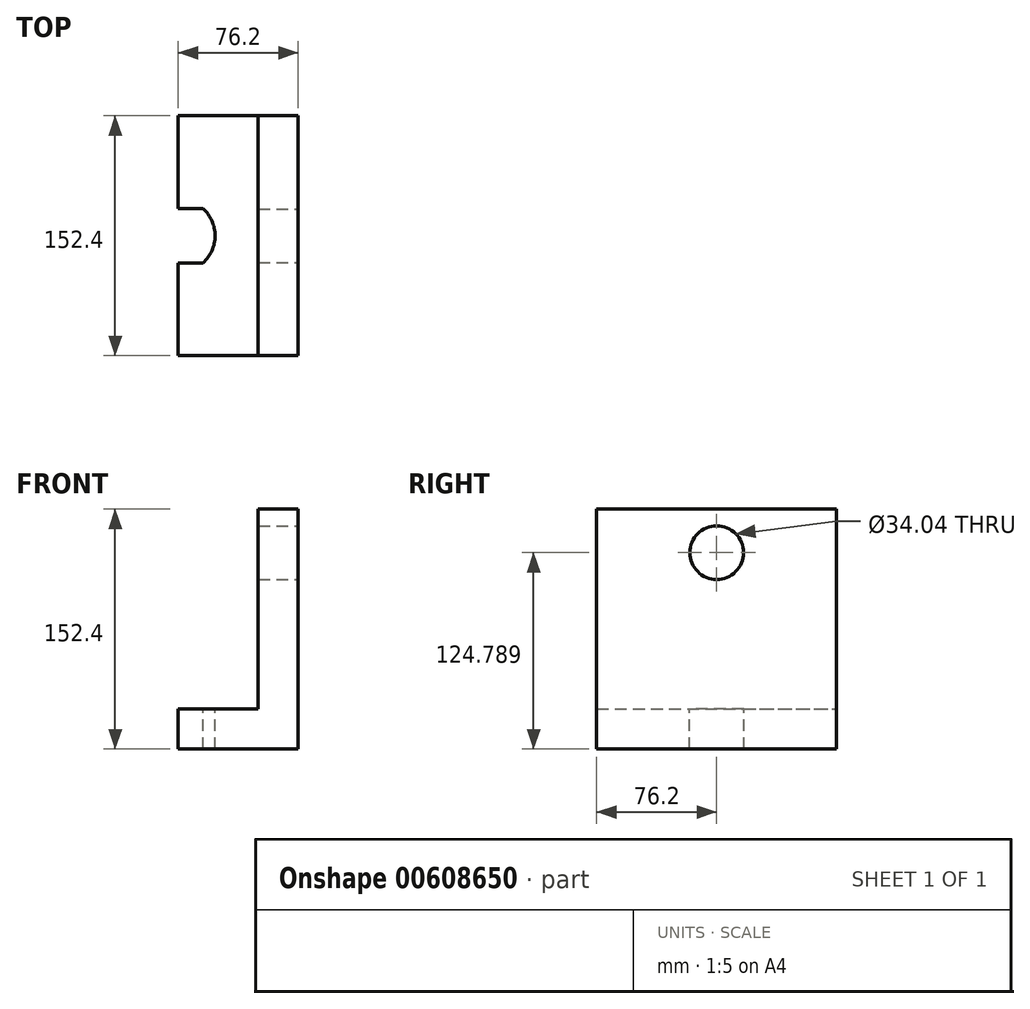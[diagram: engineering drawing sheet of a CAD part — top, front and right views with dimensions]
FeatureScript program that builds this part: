
annotation { "Feature Type Name" : "Feature", "Feature Type Description" : "" }
export const myFeature = defineFeature(function(context is Context, id is Id, definition is map)
    precondition{}
    {
        {
            var Q0;
            Q0=qCreatedBy(makeId("Front.planeOp"),FACE);
            var sketch = newSketch(context, id + "F0", { "sketchPlane" : qUnion([Q0])});
            skLineSegment(sketch, "E0", {"start": v(0, 152.4) * mm, "end": v(-25.4, 152.4) * mm});
            skLineSegment(sketch, "E1", {"start": v(-25.4, 25.4) * mm, "end": v(-76.2, 25.4) * mm});
            skLineSegment(sketch, "E2", {"start": v(-76.2, 25.4) * mm, "end": v(-76.2, 0) * mm});
            skLineSegment(sketch, "E3", {"start": v(-76.2, 0) * mm, "end": v(0, 0) * mm});
            skLineSegment(sketch, "E4", {"start": v(0, 0) * mm, "end": v(0, 152.4) * mm});
            skLineSegment(sketch, "E5", {"start": v(-25.4, 25.4) * mm, "end": v(-25.4, 152.4) * mm});
            skSolve(sketch);
        }
        {
            var Q0;
            Q0 = qSketchRegion(id + "F0", true);
            extrude(context, id + "F1", {"entities" : qUnion([Q0]), "endBound" : BoundingType.SYMMETRIC, "depth" : 152.4 * mm, "offsetDistance" : 25.4 * mm});
        }
        {
            var Q0;
            Q0=makeQuery(id+"F1.opExtrude","SWEPT_FACE",FACE,{"disambiguationData":[OSD([sQuery(id+"F0.wireOp",EDGE,"E4")])]});
            var sketch = newSketch(context, id + "F2", { "sketchPlane" : qUnion([Q0])});
            skCircle(sketch, "E6", {"center": v(0, 124.79) * mm, "radius": 17.02 * mm});
            skSolve(sketch);
        }
        {
            var Q0;
            Q0=makeQuery(id+"F2.imprint","IMPRINT",FACE,{"disambiguationData":[TD([[makeQuery(id+"F2.imprint","IMPRINT",EDGE,{"derivedFrom":sQuery(id+"F2.wireOp",EDGE,"E6")}),1.0]])]});
            extrude(context, id + "F3", {"entities" : qUnion([Q0]), "operationType" : NewBodyOperationType.REMOVE, "oppositeDirection" : true, "depth" : 38.1 * mm, "offsetDistance" : 25.4 * mm});
        }
        {
            var Q0;
            Q0=makeQuery(id+"F1.opExtrude","SWEPT_FACE",FACE,{"disambiguationData":[OSD([sQuery(id+"F0.wireOp",EDGE,"E1")])]});
            var sketch = newSketch(context, id + "F4", { "sketchPlane" : qUnion([Q0])});
            skArc(sketch, "E7", {"start": v(-60.4, -17.3) * mm, "mid": v(-52.77, 0) * mm, "end": v(-60.4, 17.3) * mm});
            skLineSegment(sketch, "E8", {"start": v(-60.4, 17.3) * mm, "end": v(-76.2, 17.3) * mm});
            skLineSegment(sketch, "E9", {"start": v(-60.4, -17.3) * mm, "end": v(-76.2, -17.3) * mm});
            skSolve(sketch);
        }
        {
            var Q0;
            Q0=makeQuery(id+"F4.imprint","IMPRINT",FACE,{"disambiguationData":[TD([[makeQuery(id+"F4.imprint","IMPRINT",EDGE,{"derivedFrom":sQuery(id+"F4.wireOp",EDGE,"E7")}),1.0]])]});
            extrude(context, id + "F5", {"entities" : qUnion([Q0]), "operationType" : NewBodyOperationType.REMOVE, "endBound" : BoundingType.SYMMETRIC, "oppositeDirection" : true, "depth" : 50.8 * mm, "offsetDistance" : 25.4 * mm});
        }
    });
